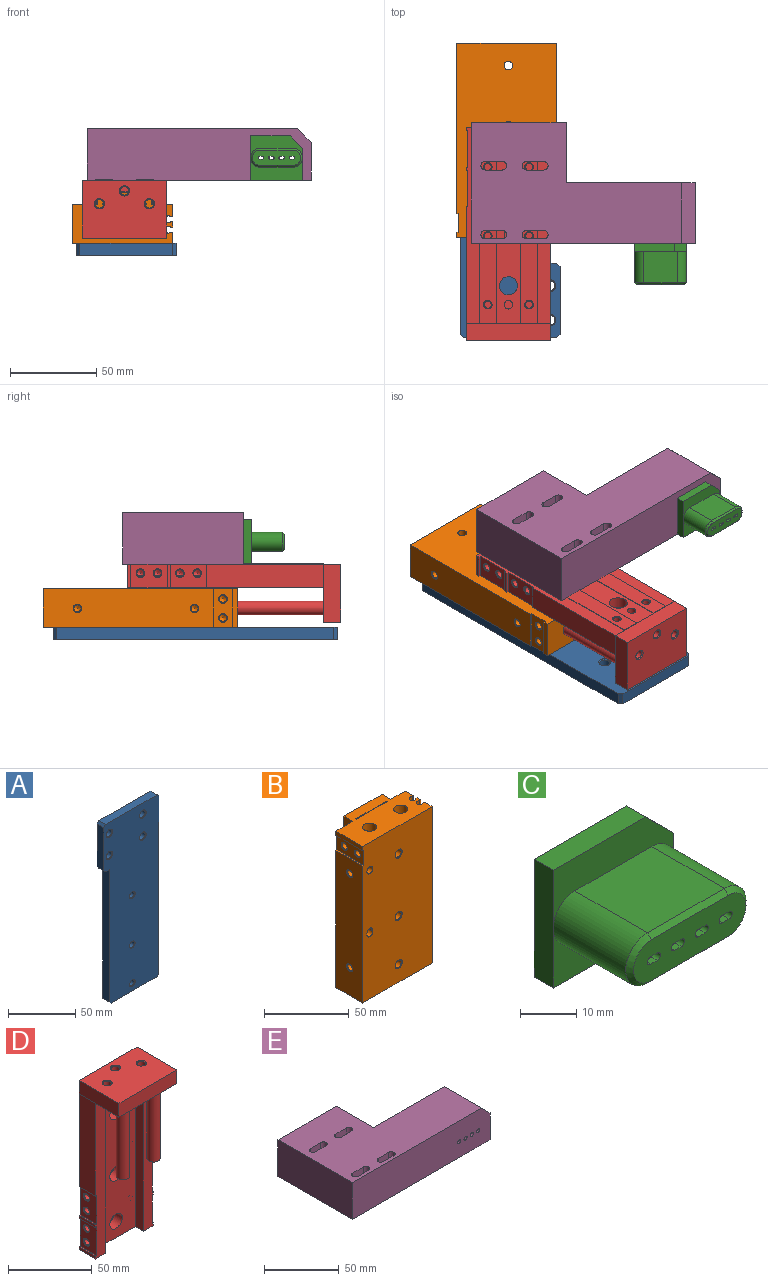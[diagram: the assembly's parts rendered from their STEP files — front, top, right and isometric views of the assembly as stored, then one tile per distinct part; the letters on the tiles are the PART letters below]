
ASSEMBLY  parts=5 mates=8
PART A: 27 faces, bbox 58x7x165 mm
  f0: plane 48x7mm, normal (0,0,-1), area 336mm2, adj f1,f2,f25,f26
  f1: plane 165x58mm, normal (0,-1,0), area 8589.2mm2, adj f0,f3,f4,f5,f10,f11,f15,f16
  f2: plane 165x58mm, normal (0,1,0), area 8656mm2, adj f0,f3,f4,f5,f6,f7,f8,f9
  f3: plane 54x7mm, normal (0,0,1), area 378mm2, adj f1,f2,f23,f24
  f4: plane 39x7mm, normal (-1,0,0), area 273mm2, adj f1,f2,f22,f23
  f5: plane 161x7mm, normal (1,0,0), area 1127mm2, adj f1,f2,f24,f25
  f6: cylinder r=3mm len=6.5mm, axis (0,-1,0), area 122.5mm2, adj f2,f17
  f7: cylinder r=3mm len=6.5mm, axis (0,-1,0), area 122.5mm2, adj f2,f16
  f8: cylinder r=3mm len=6.5mm, axis (0,-1,0), area 122.5mm2, adj f2,f15
  f9: cylinder r=3mm len=6.5mm, axis (0,-1,0), area 122.5mm2, adj f2,f18
  f10: plane 120x7mm, normal (-1,0,0), area 840mm2, adj f1,f2,f11,f26
  f11: plane 7x4mm, normal (0,0,-1), area 28mm2, adj f1,f2,f10,f22
  f12: cylinder r=2.5mm len=6.5mm, axis (0,-1,0), area 102.1mm2, adj f2,f19
  f13: cylinder r=2.5mm len=6.5mm, axis (0,-1,0), area 102.1mm2, adj f2,f20
  f14: cylinder r=2.5mm len=6.5mm, axis (0,-1,0), area 102.1mm2, adj f2,f21
  f15: cone r=3mm half-angle=45deg, axis (0,-1,0), area 14.4mm2, adj f1,f8
  f16: cone r=3mm half-angle=45deg, axis (0,-1,0), area 14.4mm2, adj f1,f7
  f17: cone r=3mm half-angle=45deg, axis (0,-1,0), area 14.4mm2, adj f1,f6
  f18: cone r=3mm half-angle=45deg, axis (0,-1,0), area 14.4mm2, adj f1,f9
  f19: cone r=2.5mm half-angle=45deg, axis (0,-1,0), area 12.2mm2, adj f1,f12
  f20: cone r=2.5mm half-angle=45deg, axis (0,-1,0), area 12.2mm2, adj f1,f13
  f21: cone r=2.5mm half-angle=45deg, axis (0,-1,0), area 12.2mm2, adj f1,f14
  f22: plane 7x2mm, normal (-0.71,0,-0.71), area 19.8mm2, adj f1,f2,f4,f11
  f23: plane 7x2mm, normal (-0.71,0,0.71), area 19.8mm2, adj f1,f2,f3,f4
  f24: plane 7x2mm, normal (0.71,0,0.71), area 19.8mm2, adj f1,f2,f3,f5
  f25: plane 7x2mm, normal (0.71,0,-0.71), area 19.8mm2, adj f0,f1,f2,f5
  f26: plane 7x2mm, normal (-0.71,0,-0.71), area 19.8mm2, adj f0,f1,f2,f10
PART B: 67 faces, bbox 58x29.8x113 mm
  f0: cylinder r=2mm len=113mm, axis (0,0,-1), area 1036.7mm2, adj f60,f61,f65,f66
  f1: cylinder r=2mm len=113mm, axis (0,0,-1), area 1036.7mm2, adj f57,f58,f65,f66
  f2: cylinder r=2.5mm len=5mm, axis (0,1,0), area 78.5mm2, adj f48,f64
  f3: cone r=3.02mm half-angle=45deg, axis (0,-1,0), area 11.1mm2, adj f4,f64
  f4: cylinder r=2.55mm len=22.05mm, axis (0,-1,0), area 353.3mm2, adj f3,f41
  f5: cone r=3.02mm half-angle=45deg, axis (0,-1,0), area 11.1mm2, adj f6,f64
  f6: cylinder r=2.55mm len=22.05mm, axis (0,-1,0), area 353.3mm2, adj f5,f41
  f7: cone r=3.02mm half-angle=45deg, axis (0,-1,0), area 11.1mm2, adj f8,f64
  f8: cylinder r=2.55mm len=22.05mm, axis (0,-1,0), area 353.3mm2, adj f7,f41
  f9: cylinder r=4.75mm len=9.5mm, axis (0,-1,0), area 202.9mm2, adj f50,f53
  f10: cone r=1.03mm half-angle=60deg, axis (0,0,-1), area 15.5mm2, adj f11
  f11: cylinder r=2.06mm len=4.13mm, axis (0,0,1), area 46.3mm2, adj f10,f12
  f12: cone r=2.53mm half-angle=45deg, axis (0,0,-1), area 8.8mm2, adj f11,f65
  f13: cone r=1.03mm half-angle=60deg, axis (0,0,-1), area 15.5mm2, adj f14
  f14: cylinder r=2.06mm len=4.13mm, axis (0,0,1), area 46.3mm2, adj f13,f15
  f15: cone r=2.53mm half-angle=45deg, axis (0,0,-1), area 8.8mm2, adj f14,f65
  f16: cone r=1.03mm half-angle=60deg, axis (0,0,-1), area 15.5mm2, adj f17
  f17: cylinder r=2.06mm len=4.13mm, axis (0,0,1), area 46.3mm2, adj f16,f18
  f18: cone r=2.53mm half-angle=45deg, axis (0,0,-1), area 8.8mm2, adj f17,f65
  f19: cone r=1.03mm half-angle=60deg, axis (0,0,-1), area 15.5mm2, adj f20
  f20: cylinder r=2.06mm len=4.13mm, axis (0,0,1), area 46.3mm2, adj f19,f21
  f21: cone r=2.53mm half-angle=45deg, axis (0,0,-1), area 8.8mm2, adj f20,f65
  f22: cone r=2.53mm half-angle=45deg, axis (-1,0,0), area 8.8mm2, adj f23,f39
  f23: cylinder r=2.06mm len=8.07mm, axis (-1,0,0), area 104.6mm2, adj f22,f24
  f24: cone r=1.03mm half-angle=60deg, axis (-1,0,0), area 15.5mm2, adj f23
  f25: cone r=2.53mm half-angle=45deg, axis (-1,0,0), area 8.8mm2, adj f26,f39
  f26: cylinder r=2.06mm len=8.07mm, axis (-1,0,0), area 104.6mm2, adj f25,f27
  f27: cone r=1.03mm half-angle=60deg, axis (-1,0,0), area 15.5mm2, adj f26
  f28: cone r=2.53mm half-angle=45deg, axis (-1,0,0), area 8.8mm2, adj f29,f63
  f29: cylinder r=2.06mm len=7.07mm, axis (-1,0,0), area 91.7mm2, adj f28,f30
  f30: cone r=1.03mm half-angle=60deg, axis (-1,0,0), area 15.5mm2, adj f29
  f31: cone r=2.53mm half-angle=45deg, axis (-1,0,0), area 8.8mm2, adj f32,f63
  f32: cylinder r=2.06mm len=7.07mm, axis (-1,0,0), area 91.7mm2, adj f31,f33
  f33: cone r=1.03mm half-angle=60deg, axis (-1,0,0), area 15.5mm2, adj f32
  f34: cylinder r=4.2mm len=51mm, axis (0,0,-1), area 1345.9mm2, adj f37,f66
  f35: cylinder r=4.2mm len=51mm, axis (0,0,-1), area 1345.9mm2, adj f36,f66
  f36: plane 8.4x8.4mm, normal (0,0,1), area 55.4mm2, adj f35
  f37: plane 8.4x8.4mm, normal (0,0,1), area 55.4mm2, adj f34
  f38: plane 22.5x1mm, normal (0,0,-1), area 22.5mm2, adj f39,f41,f42,f64
  f39: plane 22.5x11mm, normal (-1,0,0), area 208.2mm2, adj f22,f25,f38,f40,f41,f64
  f40: plane 22.5x1mm, normal (0,0,1), area 22.5mm2, adj f39,f41,f63,f64
  f41: plane 113x58mm, normal (0,1,0), area 6115.7mm2, adj f4,f6,f8,f38,f39,f40,f42,f49
  f42: plane 22.5x3mm, normal (-1,0,0), area 67.5mm2, adj f38,f41,f64,f66
  f43: cylinder r=2.5mm len=5mm, axis (0,1,0), area 39.3mm2, adj f44,f46,f47,f64
  f44: plane 5x1mm, normal (-1,0,0), area 5mm2, adj f43,f45,f47,f64
  f45: cylinder r=2.5mm len=5mm, axis (0,1,0), area 39.3mm2, adj f44,f46,f47,f64
  f46: plane 5x1mm, normal (1,0,0), area 5mm2, adj f43,f45,f47,f64
  f47: plane 6x5mm, normal (0,-1,0), area 24.6mm2, adj f43,f44,f45,f46
  f48: plane 5x5mm, normal (0,-1,0), area 19.6mm2, adj f2
  f49: plane 61x0.5mm, normal (1,0,0), area 30.5mm2, adj f41,f50,f55,f66
  f50: plane 61x25.8mm, normal (0,-1,0), area 1502.9mm2, adj f9,f49,f51,f55,f66
  f51: plane 61x0.5mm, normal (-1,0,0), area 30.5mm2, adj f41,f50,f55,f66
  f52: plane 61x7.3mm, normal (1,0,0), area 445.3mm2, adj f41,f53,f55,f66
  f53: plane 61x31.8mm, normal (0,1,0), area 1868.9mm2, adj f9,f52,f54,f55,f66
  f54: plane 61x7.3mm, normal (-1,0,0), area 445.3mm2, adj f41,f53,f55,f66
  f55: plane 31.8x7.3mm, normal (0,0,-1), area 219.2mm2, adj f41,f49,f50,f51,f52,f53,f54
  f56: plane 113x6.5mm, normal (1,0,0), area 734.5mm2, adj f57,f64,f65,f66
  f57: plane 113x1.18mm, normal (0,1,0), area 133mm2, adj f1,f56,f65,f66
  f58: plane 113x1.18mm, normal (0,-1,0), area 133mm2, adj f1,f59,f65,f66
  f59: plane 113x3mm, normal (1,0,0), area 339mm2, adj f58,f60,f65,f66
  f60: plane 113x1.18mm, normal (0,1,0), area 133mm2, adj f0,f59,f65,f66
  f61: plane 113x1.18mm, normal (0,-1,0), area 133mm2, adj f0,f62,f65,f66
  f62: plane 113x7mm, normal (1,0,0), area 791mm2, adj f41,f61,f65,f66
  f63: plane 99x22.5mm, normal (-1,0,0), area 2188.2mm2, adj f28,f31,f40,f41,f64,f65
  f64: plane 113x58mm, normal (0,-1,0), area 6413.9mm2, adj f2,f3,f5,f7,f38,f39,f40,f42
  f65: plane 58x22.5mm, normal (0,0,-1), area 1197.1mm2, adj f0,f1,f12,f15,f18,f21,f41,f56
  f66: plane 58x29.8mm, normal (0,0,1), area 1384mm2, adj f0,f1,f34,f35,f41,f42,f49,f50
PART C: 46 faces, bbox 30.2x24x25.6 mm
  f0: cylinder r=2.45mm len=16mm, axis (0,-1,0), area 246.3mm2, adj f17,f41
  f1: cylinder r=2.45mm len=16mm, axis (0,-1,0), area 246.3mm2, adj f18,f41
  f2: cylinder r=2.45mm len=16mm, axis (0,-1,0), area 246.3mm2, adj f19,f41
  f3: cylinder r=2.45mm len=16mm, axis (0,-1,0), area 246.3mm2, adj f20,f41
  f4: plane 30.2x12.65mm, normal (0,-1,0), area 205.7mm2, adj f5,f6,f8,f11,f12,f14,f15
  f5: plane 23.2x4.8mm, normal (0,0,1), area 111.4mm2, adj f4,f6,f10,f11
  f6: plane 25.6x4.8mm, normal (-1,0,0), area 122.9mm2, adj f4,f5,f7,f9,f10
  f7: plane 30.2x4.8mm, normal (0,0,-1), area 145mm2, adj f6,f8,f9,f10
  f8: plane 18.6x4.8mm, normal (1,0,0), area 89.3mm2, adj f4,f7,f9,f10,f11
  f9: plane 30.2x12.95mm, normal (0,-1,0), area 239.2mm2, adj f6,f7,f8,f12,f13,f14
  f10: plane 30.2x25.6mm, normal (0,1,0), area 569.4mm2, adj f5,f6,f7,f8,f11,f42,f43,f44
  f11: plane 7x7mm, normal (0.71,0,0.71), area 47.5mm2, adj f4,f5,f8,f10
  f12: cylinder r=5.45mm len=18.2mm, axis (0,1,0), area 311.6mm2, adj f4,f9,f13,f15,f22
  f13: plane 19.3x18.2mm, normal (0,0,-1), area 351.3mm2, adj f9,f12,f14,f24
  f14: cylinder r=5.45mm len=18.2mm, axis (0,1,0), area 311.6mm2, adj f4,f9,f13,f15,f23
  f15: plane 19.3x18.2mm, normal (0,0,1), area 351.3mm2, adj f4,f12,f14,f21
  f16: plane 28.2x8.9mm, normal (0,-1,0), area 215.1mm2, adj f21,f22,f23,f24,f25,f26,f27,f28
  f17: plane 4.9x4.9mm, normal (0,1,0), area 14.1mm2, adj f0,f37,f38,f39,f40
  f18: plane 4.9x4.9mm, normal (0,1,0), area 14.1mm2, adj f1,f33,f34,f35,f36
  f19: plane 4.9x4.9mm, normal (0,1,0), area 14.1mm2, adj f2,f29,f30,f31,f32
  f20: plane 4.9x4.9mm, normal (0,1,0), area 14.1mm2, adj f3,f25,f26,f27,f28
  f21: plane 19.3x1mm, normal (0,-0.71,0.71), area 27.3mm2, adj f15,f16,f22,f23
  f22: cone r=4.45mm half-angle=45deg, axis (0,1,0), area 22mm2, adj f12,f16,f21,f24
  f23: cone r=4.45mm half-angle=45deg, axis (0,1,0), area 22mm2, adj f14,f16,f21,f24
  f24: plane 19.3x1mm, normal (0,-0.71,-0.71), area 27.3mm2, adj f13,f16,f22,f23
  f25: plane 2x1.7mm, normal (0,0,1), area 3.4mm2, adj f16,f20,f26,f28
  f26: cylinder r=0.8mm len=2mm, axis (0,1,0), area 5mm2, adj f16,f20,f25,f27
  f27: plane 2x1.7mm, normal (0,0,-1), area 3.4mm2, adj f16,f20,f26,f28
  f28: cylinder r=0.8mm len=2mm, axis (0,1,0), area 5mm2, adj f16,f20,f25,f27
  f29: cylinder r=0.8mm len=2mm, axis (0,1,0), area 5mm2, adj f16,f19,f30,f32
  f30: plane 2x1.7mm, normal (0,0,1), area 3.4mm2, adj f16,f19,f29,f31
  f31: cylinder r=0.8mm len=2mm, axis (0,1,0), area 5mm2, adj f16,f19,f30,f32
  f32: plane 2x1.7mm, normal (0,0,-1), area 3.4mm2, adj f16,f19,f29,f31
  f33: cylinder r=0.8mm len=2mm, axis (0,1,0), area 5mm2, adj f16,f18,f34,f36
  f34: plane 2x1.7mm, normal (0,0,1), area 3.4mm2, adj f16,f18,f33,f35
  f35: cylinder r=0.8mm len=2mm, axis (0,1,0), area 5mm2, adj f16,f18,f34,f36
  f36: plane 2x1.7mm, normal (0,0,-1), area 3.4mm2, adj f16,f18,f33,f35
  f37: cylinder r=0.8mm len=2mm, axis (0,1,0), area 5mm2, adj f16,f17,f38,f40
  f38: plane 2x1.7mm, normal (0,0,1), area 3.4mm2, adj f16,f17,f37,f39
  f39: cylinder r=0.8mm len=2mm, axis (0,1,0), area 5mm2, adj f16,f17,f38,f40
  f40: plane 2x1.7mm, normal (0,0,-1), area 3.4mm2, adj f16,f17,f37,f39
  f41: plane 25.5x7.5mm, normal (0,1,0), area 103.7mm2, adj f0,f1,f2,f3,f42,f43,f44,f45
  f42: cylinder r=3.75mm len=7.5mm, axis (0,1,0), area 70.7mm2, adj f10,f41,f43,f45
  f43: plane 18x6mm, normal (0,0,1), area 108mm2, adj f10,f41,f42,f44
  f44: cylinder r=3.75mm len=7.5mm, axis (0,1,0), area 70.7mm2, adj f10,f41,f43,f45
  f45: plane 18x6mm, normal (0,0,-1), area 108mm2, adj f10,f41,f42,f44
PART D: 108 faces, bbox 49x34x124 mm
  f0: cone r=2.53mm half-angle=45deg, axis (1,0,0), area 8.8mm2, adj f1,f89
  f1: cylinder r=2.06mm len=6.27mm, axis (1,0,0), area 81.3mm2, adj f0,f2
  f2: cone r=1.03mm half-angle=60deg, axis (1,0,0), area 15.5mm2, adj f1
  f3: cone r=2.53mm half-angle=45deg, axis (1,0,0), area 8.8mm2, adj f4,f89
  f4: cylinder r=2.06mm len=6.27mm, axis (1,0,0), area 81.3mm2, adj f3,f5
  f5: cone r=1.03mm half-angle=60deg, axis (1,0,0), area 15.5mm2, adj f4
  f6: cone r=2.53mm half-angle=45deg, axis (1,0,0), area 8.8mm2, adj f7,f79
  f7: cylinder r=2.06mm len=6.27mm, axis (1,0,0), area 81.3mm2, adj f6,f8
  f8: cone r=1.03mm half-angle=60deg, axis (1,0,0), area 15.5mm2, adj f7
  f9: cone r=2.53mm half-angle=45deg, axis (1,0,0), area 8.8mm2, adj f10,f79
  f10: cylinder r=2.06mm len=6.27mm, axis (1,0,0), area 81.3mm2, adj f9,f11
  f11: cone r=1.03mm half-angle=60deg, axis (1,0,0), area 15.5mm2, adj f10
  f12: cone r=1.03mm half-angle=60deg, axis (-1,0,0), area 15.5mm2, adj f13
  f13: cylinder r=2.06mm len=6.27mm, axis (1,0,0), area 81.3mm2, adj f12,f14
  f14: cone r=2.53mm half-angle=45deg, axis (-1,0,0), area 8.8mm2, adj f13,f92
  f15: cone r=1.03mm half-angle=60deg, axis (-1,0,0), area 15.5mm2, adj f16
  f16: cylinder r=2.06mm len=6.27mm, axis (1,0,0), area 81.3mm2, adj f15,f17
  f17: cone r=2.53mm half-angle=45deg, axis (-1,0,0), area 8.8mm2, adj f16,f92
  f18: cone r=1.03mm half-angle=60deg, axis (-1,0,0), area 15.5mm2, adj f19
  f19: cylinder r=2.06mm len=6.27mm, axis (1,0,0), area 81.3mm2, adj f18,f20
  f20: cone r=2.53mm half-angle=45deg, axis (-1,0,0), area 8.8mm2, adj f19,f84
  f21: cone r=1.03mm half-angle=60deg, axis (-1,0,0), area 15.5mm2, adj f22
  f22: cylinder r=2.06mm len=6.27mm, axis (1,0,0), area 81.3mm2, adj f21,f23
  f23: cone r=2.53mm half-angle=45deg, axis (-1,0,0), area 8.8mm2, adj f22,f84
  f24: cone r=2.98mm half-angle=45deg, axis (0,0,1), area 13.1mm2, adj f25,f75
  f25: cylinder r=2.46mm len=8.92mm, axis (0,0,1), area 137.9mm2, adj f24,f26
  f26: cone r=2.98mm half-angle=45deg, axis (0,0,-1), area 21mm2, adj f25,f69,f70,f76
  f27: cone r=2.98mm half-angle=45deg, axis (0,0,1), area 13.1mm2, adj f28,f75
  f28: cylinder r=2.46mm len=8.92mm, axis (0,0,1), area 137.9mm2, adj f27,f29
  f29: cone r=2.98mm half-angle=45deg, axis (0,0,-1), area 15.5mm2, adj f28,f67,f68,f76,f95
  f30: cone r=2.98mm half-angle=45deg, axis (0,0,1), area 13.1mm2, adj f31,f75
  f31: cylinder r=2.46mm len=8.92mm, axis (0,0,1), area 137.9mm2, adj f30,f32
  f32: cone r=2.98mm half-angle=45deg, axis (0,0,-1), area 15.5mm2, adj f31,f65,f66,f76,f96
  f33: cylinder r=5.25mm len=10.5mm, axis (0,-1,0), area 221mm2, adj f70,f101
  f34: cylinder r=5.25mm len=10.5mm, axis (0,-1,0), area 221mm2, adj f70,f101
  f35: cylinder r=5.25mm len=10.5mm, axis (0,-1,0), area 221mm2, adj f70,f101
  f36: cone r=2.53mm half-angle=45deg, axis (0,1,0), area 8.8mm2, adj f37,f103
  f37: cylinder r=2.06mm len=5.77mm, axis (0,1,0), area 74.8mm2, adj f36,f64
  f38: cone r=2.53mm half-angle=45deg, axis (0,1,0), area 8.8mm2, adj f39,f99
  f39: cylinder r=2.06mm len=5.77mm, axis (0,1,0), area 74.8mm2, adj f38,f63
  f40: cone r=2.53mm half-angle=45deg, axis (0,1,0), area 8.8mm2, adj f41,f103
  f41: cylinder r=2.06mm len=6.07mm, axis (0,1,0), area 78.7mm2, adj f40,f62
  f42: cone r=2.53mm half-angle=45deg, axis (0,1,0), area 8.8mm2, adj f43,f99
  f43: cylinder r=2.06mm len=6.07mm, axis (0,1,0), area 78.7mm2, adj f42,f61
  f44: cone r=2.53mm half-angle=45deg, axis (0,1,0), area 8.8mm2, adj f45,f103
  f45: cylinder r=2.06mm len=6.07mm, axis (0,1,0), area 78.7mm2, adj f44,f60
  f46: cone r=2.53mm half-angle=45deg, axis (0,1,0), area 8.8mm2, adj f47,f99
  f47: cylinder r=2.06mm len=6.07mm, axis (0,1,0), area 78.7mm2, adj f46,f59
  f48: cylinder r=2.5mm len=5mm, axis (0,-1,0), area 78.5mm2, adj f58,f101
  f49: cylinder r=4mm len=53mm, axis (0,0,-1), area 1332mm2, adj f52,f76
  f50: cylinder r=4mm len=53mm, axis (0,0,-1), area 1332mm2, adj f51,f76
  f51: plane 8x8mm, normal (0,0,-1), area 50.3mm2, adj f50
  f52: plane 8x8mm, normal (0,0,-1), area 50.3mm2, adj f49
  f53: cylinder r=2.5mm len=5mm, axis (0,-1,0), area 39.3mm2, adj f54,f56,f57,f101
  f54: plane 5x1mm, normal (-1,0,0), area 5mm2, adj f53,f55,f57,f101
  f55: cylinder r=2.5mm len=5mm, axis (0,-1,0), area 39.3mm2, adj f54,f56,f57,f101
  f56: plane 5x1mm, normal (1,0,0), area 5mm2, adj f53,f55,f57,f101
  f57: plane 6x5mm, normal (0,1,0), area 24.6mm2, adj f53,f54,f55,f56
  f58: plane 5x5mm, normal (0,1,0), area 19.6mm2, adj f48
  f59: plane 4.13x4.13mm, normal (0,1,0), area 13.4mm2, adj f47
  f60: plane 4.13x4.13mm, normal (0,1,0), area 13.4mm2, adj f45
  f61: plane 4.13x4.13mm, normal (0,1,0), area 13.4mm2, adj f43
  f62: plane 4.13x4.13mm, normal (0,1,0), area 13.4mm2, adj f41
  f63: plane 4.13x4.13mm, normal (0,1,0), area 13.4mm2, adj f39
  f64: plane 4.13x4.13mm, normal (0,1,0), area 13.4mm2, adj f37
  f65: plane 3.11x1.9mm, normal (0,0,1), area 4.2mm2, adj f32,f66,f96
  f66: plane 114x7mm, normal (-1,0,0), area 796.6mm2, adj f32,f65,f70,f76,f96,f106
  f67: plane 3.11x1.9mm, normal (0,0,1), area 4.2mm2, adj f29,f68,f95
  f68: plane 114x8.4mm, normal (0,-1,0), area 914.8mm2, adj f29,f67,f76,f83,f84,f85,f87,f91
  f69: plane 7x4mm, normal (0,0,1), area 22.7mm2, adj f26,f70
  f70: plane 114.01x32.21mm, normal (0,-1,0), area 3407.8mm2, adj f26,f33,f34,f35,f66,f69,f76,f95
  f71: plane 48.98x10mm, normal (0,1,0), area 489.8mm2, adj f72,f74,f75,f107
  f72: plane 33.69x10mm, normal (1,0,0), area 336.9mm2, adj f71,f73,f75,f76,f107
  f73: plane 48.98x10mm, normal (0,-1,0), area 489.8mm2, adj f72,f74,f75,f76
  f74: plane 33.69x10mm, normal (-1,0,0), area 336.9mm2, adj f71,f73,f75,f76,f107
  f75: plane 48.98x33.69mm, normal (0,0,1), area 1565.3mm2, adj f24,f27,f30,f71,f72,f73,f74
  f76: plane 48.98x27mm, normal (0,0,-1), area 1041.8mm2, adj f26,f29,f32,f49,f50,f66,f68,f70
  f77: plane 13.7x1mm, normal (0,0,-1), area 13.7mm2, adj f79,f80,f82,f96
  f78: plane 13.7x1mm, normal (0,0,1), area 13.7mm2, adj f79,f80,f81,f96
  f79: plane 21x13.7mm, normal (1,0,0), area 248.4mm2, adj f6,f9,f77,f78,f80,f96
  f80: plane 114x7.5mm, normal (0,1,0), area 813mm2, adj f77,f78,f79,f81,f82,f88,f89,f90
  f81: plane 13.7x2mm, normal (1,0,0), area 27.4mm2, adj f78,f80,f96,f106
  f82: plane 13.7x2mm, normal (1,0,0), area 27.4mm2, adj f77,f80,f88,f96
  f83: plane 13.7x1mm, normal (0,0,-1), area 13.7mm2, adj f68,f84,f86,f87
  f84: plane 21x13.7mm, normal (-1,0,0), area 248.4mm2, adj f20,f23,f68,f83,f85,f86
  f85: plane 13.7x1mm, normal (0,0,1), area 13.7mm2, adj f68,f84,f86,f105
  f86: plane 114x7.5mm, normal (0,1,0), area 813mm2, adj f83,f84,f85,f87,f91,f92,f93,f94
  f87: plane 13.7x2mm, normal (-1,0,0), area 27.4mm2, adj f68,f83,f86,f93
  f88: plane 13.7x1mm, normal (0,0,1), area 13.7mm2, adj f80,f82,f89,f96
  f89: plane 21x13.7mm, normal (1,0,0), area 248.4mm2, adj f0,f3,f80,f88,f90,f96
  f90: plane 13.7x1mm, normal (0,0,-1), area 13.7mm2, adj f80,f89,f96,f97
  f91: plane 13.7x1mm, normal (0,0,-1), area 13.7mm2, adj f68,f86,f92,f94
  f92: plane 21x13.7mm, normal (-1,0,0), area 248.4mm2, adj f14,f17,f68,f86,f91,f93
  f93: plane 13.7x1mm, normal (0,0,1), area 13.7mm2, adj f68,f86,f87,f92
  f94: plane 68x13.7mm, normal (-1,0,0), area 931.6mm2, adj f68,f86,f91,f107
  f95: plane 114x7mm, normal (1,0,0), area 796.6mm2, adj f29,f67,f68,f70,f76,f106
  f96: plane 114x8.4mm, normal (0,-1,0), area 914.8mm2, adj f32,f65,f66,f76,f77,f78,f79,f81
  f97: plane 68x13.7mm, normal (1,0,0), area 931.6mm2, adj f80,f90,f96,f107
  f98: plane 114x0.3mm, normal (1,0,0), area 34.2mm2, adj f80,f99,f106,f107
  f99: plane 114x10mm, normal (0,1,0), area 1081.1mm2, adj f38,f42,f46,f98,f100,f106,f107
  f100: plane 114x0.3mm, normal (-1,0,0), area 34.2mm2, adj f99,f101,f106,f107
  f101: plane 114x14mm, normal (0,1,0), area 1292mm2, adj f33,f34,f35,f48,f53,f54,f55,f56
  f102: plane 114x0.3mm, normal (1,0,0), area 34.2mm2, adj f101,f103,f106,f107
  f103: plane 114x10mm, normal (0,1,0), area 1081.1mm2, adj f36,f40,f44,f102,f104,f106,f107
  f104: plane 114x0.3mm, normal (-1,0,0), area 34.2mm2, adj f86,f103,f106,f107
  f105: plane 13.7x2mm, normal (-1,0,0), area 27.4mm2, adj f68,f85,f86,f106
  f106: plane 49x14mm, normal (0,0,-1), area 451.9mm2, adj f66,f68,f70,f80,f81,f86,f95,f96
  f107: plane 49x14mm, normal (0,0,1), area 6.8mm2, adj f68,f71,f72,f74,f80,f86,f94,f96
PART E: 29 faces, bbox 130x70x30 mm
  f0: plane 75x30mm, normal (0,1,0), area 2190.1mm2, adj f1,f3,f4,f6,f7,f8,f9,f10
  f1: plane 122x70mm, normal (0,0,1), area 5916.5mm2, adj f0,f2,f5,f6,f11,f12,f13,f14
  f2: plane 70x30mm, normal (-1,0,0), area 2100mm2, adj f1,f3,f5,f12
  f3: plane 130x70mm, normal (0,0,-1), area 6196.5mm2, adj f0,f2,f4,f5,f11,f12,f13,f14
  f4: plane 35x22mm, normal (1,0,0), area 770mm2, adj f0,f3,f5,f6
  f5: plane 130x30mm, normal (0,-1,0), area 3840.1mm2, adj f1,f2,f3,f4,f6,f7,f8,f9
  f6: plane 35x8mm, normal (0.71,0,0.71), area 396mm2, adj f0,f1,f4,f5
  f7: cylinder r=1.5mm len=35mm, axis (0,-1,0), area 329.9mm2, adj f0,f5
  f8: cylinder r=1.49mm len=35mm, axis (0,-1,0), area 327.2mm2, adj f0,f5
  f9: cylinder r=1.48mm len=35mm, axis (0,-1,0), area 324.9mm2, adj f0,f5
  f10: cylinder r=1.5mm len=35mm, axis (0,-1,0), area 329.9mm2, adj f0,f5
  f11: plane 35x30mm, normal (1,0,0), area 1050mm2, adj f0,f1,f3,f12
  f12: plane 55x30mm, normal (0,1,0), area 1650mm2, adj f1,f2,f3,f11
  f13: cylinder r=2.5mm len=30mm, axis (0,0,1), area 235.6mm2, adj f1,f3,f14,f16
  f14: plane 30x10mm, normal (0,1,0), area 300mm2, adj f1,f3,f13,f15
  f15: cylinder r=2.5mm len=30mm, axis (0,0,1), area 235.6mm2, adj f1,f3,f14,f16
  f16: plane 30x10mm, normal (0,-1,0), area 300mm2, adj f1,f3,f13,f15
  f17: cylinder r=2.5mm len=30mm, axis (0,0,1), area 235.6mm2, adj f1,f3,f18,f20
  f18: plane 30x10mm, normal (0,1,0), area 300mm2, adj f1,f3,f17,f19
  f19: cylinder r=2.5mm len=30mm, axis (0,0,1), area 235.6mm2, adj f1,f3,f18,f20
  f20: plane 30x10mm, normal (0,-1,0), area 300mm2, adj f1,f3,f17,f19
  f21: cylinder r=2.5mm len=30mm, axis (0,0,1), area 235.6mm2, adj f1,f3,f22,f24
  f22: plane 30x10mm, normal (0,1,0), area 300mm2, adj f1,f3,f21,f23
  f23: cylinder r=2.5mm len=30mm, axis (0,0,1), area 235.6mm2, adj f1,f3,f22,f24
  f24: plane 30x10mm, normal (0,-1,0), area 300mm2, adj f1,f3,f21,f23
  f25: cylinder r=2.5mm len=30mm, axis (0,0,1), area 235.6mm2, adj f1,f3,f26,f28
  f26: plane 30x10mm, normal (0,1,0), area 300mm2, adj f1,f3,f25,f27
  f27: cylinder r=2.5mm len=30mm, axis (0,0,1), area 235.6mm2, adj f1,f3,f26,f28
  f28: plane 30x10mm, normal (0,-1,0), area 300mm2, adj f1,f3,f25,f27
PLACE A rot(axis=(0,-0.71,0.71),180deg) t=(6.64,-9.57,-145.89)mm
PLACE B rot(axis=(1,0,0),90deg) t=(21.77,-44.88,-138.89)mm
PLACE C t=(107.28,-48.23,-86.35)mm
PLACE D rot(axis=(1,0,0),90deg) t=(21.77,-92.92,-138.89)mm
PLACE E rot(axis=(1,0,0),0deg) t=(64.77,-13.23,-85.22)mm
MATE planar E.f3 <-> D.f101  axis (0,0,-1) through (55.42,-20.19,-102.19)mm
MATE parallel E.f5 <-> D.f75  axis (0,-1,0) through (64.43,-48.23,-87.28)mm
MATE cylindrical B.f3 <-> A.f12  axis (0,0,-1) through (21.77,55.12,-127.41)mm
MATE cylindrical D.f50 <-> B.f34  axis (0,1,0) through (8.77,-41.92,-127.64)mm
MATE cylindrical D.f49 <-> B.f35  axis (0,1,0) through (34.77,-68.42,-127.64)mm
MATE planar B.f64 <-> A.f1  axis (0,0,-1) through (20.96,11.71,-138.89)mm
MATE cylindrical B.f7 <-> A.f14  axis (0,0,1) through (21.77,-24.88,-116.39)mm
MATE planar E.f5 <-> C.f10  axis (0,-1,0) through (64.43,-48.23,-87.28)mm
